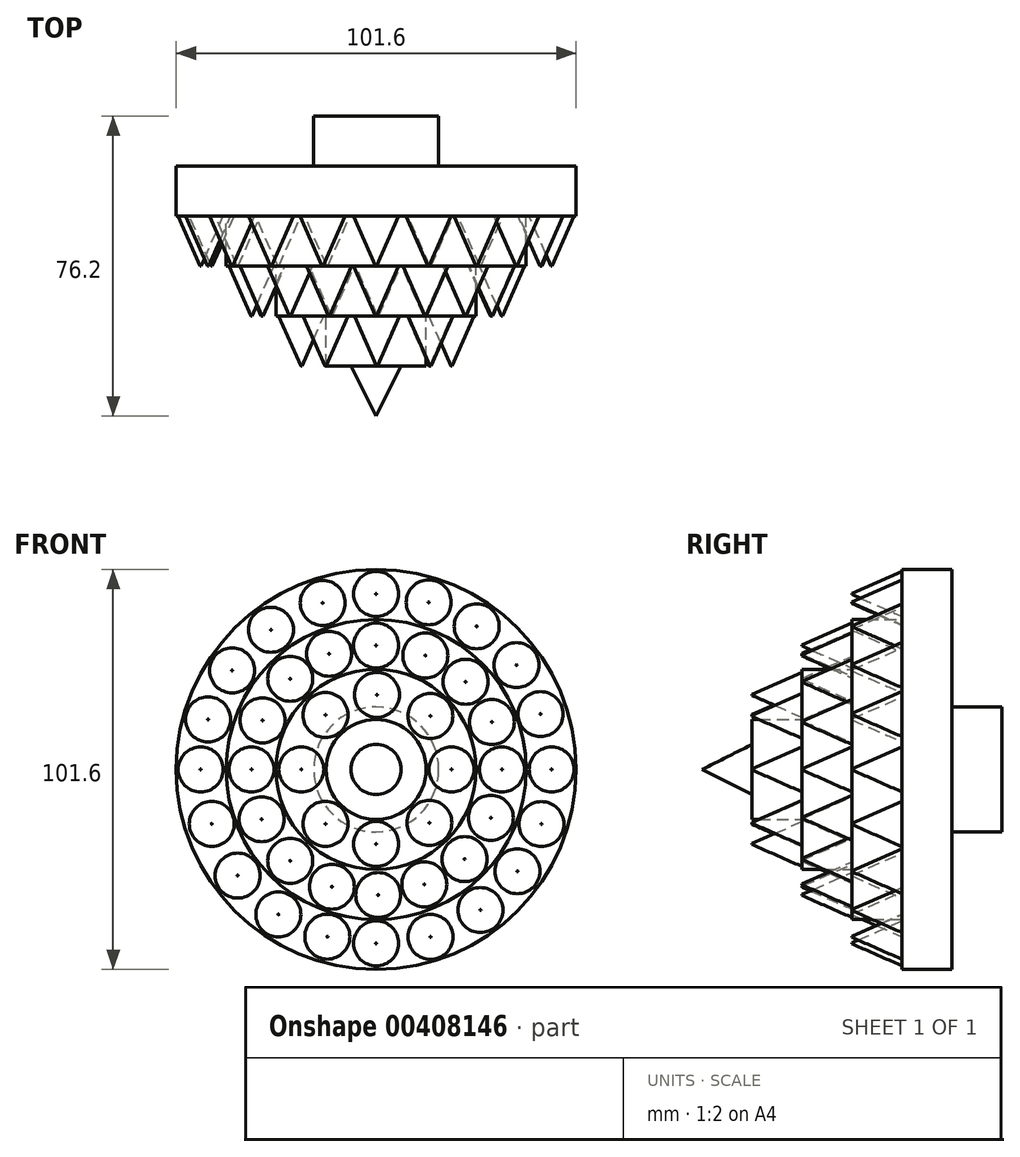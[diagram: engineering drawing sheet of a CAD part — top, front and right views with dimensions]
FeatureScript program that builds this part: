
annotation { "Feature Type Name" : "Feature", "Feature Type Description" : "" }
export const myFeature = defineFeature(function(context is Context, id is Id, definition is map)
    precondition{}
    {
        {
            var Q0;
            Q0=qCreatedBy(makeId("Front.planeOp"),FACE);
            var sketch = newSketch(context, id + "F0", { "sketchPlane" : qUnion([Q0])});
            skCircle(sketch, "E0", {"center": v(0, 0) * mm, "radius": 15.88 * mm});
            skSolve(sketch);
        }
        {
            var Q0;
            Q0=qSketchRegion(id+"F0",true);
            extrude(context, id + "F1", {"entities" : qUnion([Q0]), "depth" : 12.7 * mm});
        }
        {
            var Q0;
            Q0=makeQuery(id+"F1.opExtrude","CAP_FACE",FACE,{"disambiguationData":[OSD([sQuery(id+"F0.wireOp",EDGE,"E0")])],"isStart":false});
            var sketch = newSketch(context, id + "F2", { "sketchPlane" : qUnion([Q0])});
            skCircle(sketch, "E1", {"center": v(0, 0) * mm, "radius": 50.8 * mm});
            skSolve(sketch);
        }
        {
            var Q0;
            Q0=qSketchRegion(id+"F2",true);
            extrude(context, id + "F3", {"entities" : qUnion([Q0]), "operationType" : NewBodyOperationType.ADD, "depth" : 12.7 * mm});
        }
        {
            var Q0;
            Q0=makeQuery(id+"F3.opExtrude","CAP_FACE",FACE,{"disambiguationData":[OSD([sQuery(id+"F2.wireOp",EDGE,"E1")])],"isStart":false});
            var sketch = newSketch(context, id + "F4", { "sketchPlane" : qUnion([Q0])});
            skCircle(sketch, "E2", {"center": v(0, 0) * mm, "radius": 38.1 * mm});
            skSolve(sketch);
        }
        {
            var Q0;
            Q0=qSketchRegion(id+"F4",true);
            extrude(context, id + "F5", {"entities" : qUnion([Q0]), "operationType" : NewBodyOperationType.ADD, "depth" : 12.7 * mm});
        }
        {
            var Q0;
            Q0=makeQuery(id+"F5.opExtrude","CAP_FACE",FACE,{"disambiguationData":[OSD([sQuery(id+"F4.wireOp",EDGE,"E2")])],"isStart":false});
            var sketch = newSketch(context, id + "F6", { "sketchPlane" : qUnion([Q0])});
            skCircle(sketch, "E3", {"center": v(0, 0) * mm, "radius": 25.4 * mm});
            skSolve(sketch);
        }
        {
            var Q0;
            Q0=qSketchRegion(id+"F6",true);
            extrude(context, id + "F7", {"entities" : qUnion([Q0]), "operationType" : NewBodyOperationType.ADD, "depth" : 12.7 * mm});
        }
        {
            var Q0;
            Q0=makeQuery(id+"F7.opExtrude","CAP_FACE",FACE,{"disambiguationData":[OSD([sQuery(id+"F6.wireOp",EDGE,"E3")])],"isStart":false});
            var sketch = newSketch(context, id + "F8", { "sketchPlane" : qUnion([Q0])});
            skCircle(sketch, "E4", {"center": v(0, 0) * mm, "radius": 12.7 * mm});
            skSolve(sketch);
        }
        {
            var Q0;
            Q0=qSketchRegion(id+"F8",true);
            extrude(context, id + "F9", {"entities" : qUnion([Q0]), "operationType" : NewBodyOperationType.ADD, "depth" : 12.7 * mm});
        }
        {
            var Q0;
            Q0=makeQuery(id+"F9.opExtrude","CAP_FACE",FACE,{"disambiguationData":[OSD([sQuery(id+"F8.wireOp",EDGE,"E4")])],"isStart":false});
            var sketch = newSketch(context, id + "F10", { "sketchPlane" : qUnion([Q0])});
            skCircle(sketch, "E5", {"center": v(0, 0) * mm, "radius": 6.35 * mm});
            skSolve(sketch);
        }
        {
            var Q0;
            Q0=qSketchRegion(id+"F10",true);
            extrude(context, id + "F11", {"entities" : qUnion([Q0]), "operationType" : NewBodyOperationType.ADD, "depth" : 12.7 * mm});
        }
        {
            var Q0;
            Q0=makeQuery(id+"F11.opExtrude","CAP_EDGE",EDGE,{"disambiguationData":[OSD([sQuery(id+"F10.wireOp",EDGE,"E5")])],"isStart":false});
            chamfer(context, id + "F12", {"entities" : qUnion([Q0]), "chamferType" : ChamferType.TWO_OFFSETS, "width1" : 6.35 * mm, "oppositeDirection" : false, "width2" : 12.7 * mm, "tangentPropagation" : true});
        }
        {
            var Q0;
            Q0=makeQuery(id+"F3.opExtrude","CAP_FACE",FACE,{"disambiguationData":[OSD([sQuery(id+"F2.wireOp",EDGE,"E1")])],"isStart":false});
            var sketch = newSketch(context, id + "F13", { "sketchPlane" : qUnion([Q0])});
            skCircle(sketch, "E6", {"center": v(25.56, 36.37) * mm, "radius": 5.72 * mm});
            skCircle(sketch, "E7", {"center": v(35.65, 26.5) * mm, "radius": 5.72 * mm});
            skCircle(sketch, "E8", {"center": v(41.76, 14.06) * mm, "radius": 5.72 * mm});
            skCircle(sketch, "E9", {"center": v(44.58, 0) * mm, "radius": 5.72 * mm});
            skCircle(sketch, "E10", {"center": v(42, -13.89) * mm, "radius": 5.72 * mm});
            skCircle(sketch, "E11", {"center": v(35.89, -25.86) * mm, "radius": 5.72 * mm});
            skCircle(sketch, "E12", {"center": v(26.5, -35.73) * mm, "radius": 5.72 * mm});
            skCircle(sketch, "E13", {"center": v(13.34, 42.47) * mm, "radius": 5.72 * mm});
            skCircle(sketch, "E14", {"center": v(0, 44.59) * mm, "radius": 5.72 * mm});
            skCircle(sketch, "E15", {"center": v(0, -44.18) * mm, "radius": 5.72 * mm});
            skCircle(sketch, "E16", {"center": v(13.81, -42.54) * mm, "radius": 5.72 * mm});
            skCircle(sketch, "E17", {"center": v(-12.4, -42.47) * mm, "radius": 5.72 * mm});
            skCircle(sketch, "E18", {"center": v(-24.85, -36.84) * mm, "radius": 5.72 * mm});
            skCircle(sketch, "E19", {"center": v(-35.18, -26.98) * mm, "radius": 5.72 * mm});
            skCircle(sketch, "E20", {"center": v(-41.76, -13.82) * mm, "radius": 5.72 * mm});
            skCircle(sketch, "E21", {"center": v(-44.58, 0) * mm, "radius": 5.72 * mm});
            skCircle(sketch, "E22", {"center": v(-42.7, 12.71) * mm, "radius": 5.72 * mm});
            skCircle(sketch, "E23", {"center": v(-36.6, 25.16) * mm, "radius": 5.72 * mm});
            skCircle(sketch, "E24", {"center": v(-26.73, 35.5) * mm, "radius": 5.72 * mm});
            skCircle(sketch, "E25", {"center": v(-13.58, 42.3) * mm, "radius": 5.72 * mm});
            skSolve(sketch);
        }
        {
            var Q0;
            Q0=qSketchRegion(id+"F13",true);
            extrude(context, id + "F14", {"entities" : qUnion([Q0]), "operationType" : NewBodyOperationType.ADD, "depth" : 12.7 * mm});
        }
        {
            var Q0;
            Q0=makeQuery(id+"F14.opExtrude","CAP_EDGE",EDGE,{"disambiguationData":[OSD([sQuery(id+"F13.wireOp",EDGE,"E20")])],"isStart":false});
            var Q1;
            Q1=makeQuery(id+"F14.opExtrude","CAP_EDGE",EDGE,{"disambiguationData":[OSD([sQuery(id+"F13.wireOp",EDGE,"E21")])],"isStart":false});
            var Q2;
            Q2=makeQuery(id+"F14.opExtrude","CAP_EDGE",EDGE,{"disambiguationData":[OSD([sQuery(id+"F13.wireOp",EDGE,"E22")])],"isStart":false});
            var Q3;
            Q3=makeQuery(id+"F14.opExtrude","CAP_EDGE",EDGE,{"disambiguationData":[OSD([sQuery(id+"F13.wireOp",EDGE,"E23")])],"isStart":false});
            var Q4;
            Q4=makeQuery(id+"F14.opExtrude","CAP_EDGE",EDGE,{"disambiguationData":[OSD([sQuery(id+"F13.wireOp",EDGE,"E24")])],"isStart":false});
            var Q5;
            Q5=makeQuery(id+"F14.opExtrude","CAP_EDGE",EDGE,{"disambiguationData":[OSD([sQuery(id+"F13.wireOp",EDGE,"E25")])],"isStart":false});
            var Q6;
            Q6=makeQuery(id+"F14.opExtrude","CAP_EDGE",EDGE,{"disambiguationData":[OSD([sQuery(id+"F13.wireOp",EDGE,"E14")])],"isStart":false});
            var Q7;
            Q7=makeQuery(id+"F14.opExtrude","CAP_EDGE",EDGE,{"disambiguationData":[OSD([sQuery(id+"F13.wireOp",EDGE,"E13")])],"isStart":false});
            var Q8;
            Q8=makeQuery(id+"F14.opExtrude","CAP_EDGE",EDGE,{"disambiguationData":[OSD([sQuery(id+"F13.wireOp",EDGE,"E6")])],"isStart":false});
            var Q9;
            Q9=makeQuery(id+"F14.opExtrude","CAP_EDGE",EDGE,{"disambiguationData":[OSD([sQuery(id+"F13.wireOp",EDGE,"E7")])],"isStart":false});
            var Q10;
            Q10=makeQuery(id+"F14.opExtrude","CAP_EDGE",EDGE,{"disambiguationData":[OSD([sQuery(id+"F13.wireOp",EDGE,"E8")])],"isStart":false});
            var Q11;
            Q11=makeQuery(id+"F14.opExtrude","CAP_EDGE",EDGE,{"disambiguationData":[OSD([sQuery(id+"F13.wireOp",EDGE,"E9")])],"isStart":false});
            var Q12;
            Q12=makeQuery(id+"F14.opExtrude","CAP_EDGE",EDGE,{"disambiguationData":[OSD([sQuery(id+"F13.wireOp",EDGE,"E10")])],"isStart":false});
            var Q13;
            Q13=makeQuery(id+"F14.opExtrude","CAP_EDGE",EDGE,{"disambiguationData":[OSD([sQuery(id+"F13.wireOp",EDGE,"E11")])],"isStart":false});
            var Q14;
            Q14=makeQuery(id+"F14.opExtrude","CAP_EDGE",EDGE,{"disambiguationData":[OSD([sQuery(id+"F13.wireOp",EDGE,"E12")])],"isStart":false});
            var Q15;
            Q15=makeQuery(id+"F14.opExtrude","CAP_EDGE",EDGE,{"disambiguationData":[OSD([sQuery(id+"F13.wireOp",EDGE,"E16")])],"isStart":false});
            var Q16;
            Q16=makeQuery(id+"F14.opExtrude","CAP_EDGE",EDGE,{"disambiguationData":[OSD([sQuery(id+"F13.wireOp",EDGE,"E15")])],"isStart":false});
            var Q17;
            Q17=makeQuery(id+"F14.opExtrude","CAP_EDGE",EDGE,{"disambiguationData":[OSD([sQuery(id+"F13.wireOp",EDGE,"E17")])],"isStart":false});
            var Q18;
            Q18=makeQuery(id+"F14.opExtrude","CAP_EDGE",EDGE,{"disambiguationData":[OSD([sQuery(id+"F13.wireOp",EDGE,"E18")])],"isStart":false});
            var Q19;
            Q19=makeQuery(id+"F14.opExtrude","CAP_EDGE",EDGE,{"disambiguationData":[OSD([sQuery(id+"F13.wireOp",EDGE,"E19")])],"isStart":false});
            chamfer(context, id + "F15", {"entities" : qUnion([Q0, Q1, Q2, Q3, Q4, Q5, Q6, Q7, Q8, Q9, Q10, Q11, Q12, Q13, Q14, Q15, Q16, Q17, Q18, Q19]), "chamferType" : ChamferType.TWO_OFFSETS, "width1" : 5.6 * mm, "oppositeDirection" : false, "width2" : 12.7 * mm, "tangentPropagation" : true});
        }
        {
            var Q0;
            Q0=makeQuery(id+"F5.opExtrude","CAP_FACE",FACE,{"disambiguationData":[OSD([sQuery(id+"F4.wireOp",EDGE,"E2")])],"isStart":false});
            var sketch = newSketch(context, id + "F16", { "sketchPlane" : qUnion([Q0])});
            skCircle(sketch, "E26", {"center": v(-31.68, 0) * mm, "radius": 5.72 * mm});
            skCircle(sketch, "E27", {"center": v(0, 31.5) * mm, "radius": 5.72 * mm});
            skCircle(sketch, "E28", {"center": v(0.51, -31.9) * mm, "radius": 5.72 * mm});
            skCircle(sketch, "E29", {"center": v(31.95, 0) * mm, "radius": 5.72 * mm});
            skCircle(sketch, "E30", {"center": v(29.39, 12.04) * mm, "radius": 5.72 * mm});
            skCircle(sketch, "E31", {"center": v(22.73, 22.29) * mm, "radius": 5.72 * mm});
            skCircle(sketch, "E32", {"center": v(12.48, 28.95) * mm, "radius": 5.72 * mm});
            skCircle(sketch, "E33", {"center": v(29.13, -12.29) * mm, "radius": 5.72 * mm});
            skCircle(sketch, "E34", {"center": v(22.47, -22.79) * mm, "radius": 5.72 * mm});
            skCircle(sketch, "E35", {"center": v(12.23, -29.19) * mm, "radius": 5.72 * mm});
            skCircle(sketch, "E36", {"center": v(-11.25, -29.8) * mm, "radius": 5.72 * mm});
            skCircle(sketch, "E37", {"center": v(-21.82, -23.22) * mm, "radius": 5.72 * mm});
            skCircle(sketch, "E38", {"center": v(-29.1, -12.65) * mm, "radius": 5.72 * mm});
            skCircle(sketch, "E39", {"center": v(-28.86, 12.48) * mm, "radius": 5.72 * mm});
            skCircle(sketch, "E40", {"center": v(-21.82, 23.05) * mm, "radius": 5.72 * mm});
            skCircle(sketch, "E41", {"center": v(-11.96, 29.39) * mm, "radius": 5.72 * mm});
            skSolve(sketch);
        }
        {
            var Q0;
            Q0=qSketchRegion(id+"F16",true);
            extrude(context, id + "F17", {"entities" : qUnion([Q0]), "operationType" : NewBodyOperationType.ADD, "depth" : 12.7 * mm});
        }
        {
            var Q0;
            Q0=makeQuery(id+"F17.opExtrude","CAP_EDGE",EDGE,{"disambiguationData":[OSD([sQuery(id+"F16.wireOp",EDGE,"E33")])],"isStart":false});
            var Q1;
            Q1=makeQuery(id+"F17.opExtrude","CAP_EDGE",EDGE,{"disambiguationData":[OSD([sQuery(id+"F16.wireOp",EDGE,"E29")])],"isStart":false});
            var Q2;
            Q2=makeQuery(id+"F17.opExtrude","CAP_EDGE",EDGE,{"disambiguationData":[OSD([sQuery(id+"F16.wireOp",EDGE,"E30")])],"isStart":false});
            var Q3;
            Q3=makeQuery(id+"F17.opExtrude","CAP_EDGE",EDGE,{"disambiguationData":[OSD([sQuery(id+"F16.wireOp",EDGE,"E31")])],"isStart":false});
            var Q4;
            Q4=makeQuery(id+"F17.opExtrude","CAP_EDGE",EDGE,{"disambiguationData":[OSD([sQuery(id+"F16.wireOp",EDGE,"E32")])],"isStart":false});
            var Q5;
            Q5=makeQuery(id+"F17.opExtrude","CAP_EDGE",EDGE,{"disambiguationData":[OSD([sQuery(id+"F16.wireOp",EDGE,"E27")])],"isStart":false});
            var Q6;
            Q6=makeQuery(id+"F17.opExtrude","CAP_EDGE",EDGE,{"disambiguationData":[OSD([sQuery(id+"F16.wireOp",EDGE,"E41")])],"isStart":false});
            var Q7;
            Q7=makeQuery(id+"F17.opExtrude","CAP_EDGE",EDGE,{"disambiguationData":[OSD([sQuery(id+"F16.wireOp",EDGE,"E40")])],"isStart":false});
            var Q8;
            Q8=makeQuery(id+"F17.opExtrude","CAP_EDGE",EDGE,{"disambiguationData":[OSD([sQuery(id+"F16.wireOp",EDGE,"E39")])],"isStart":false});
            var Q9;
            Q9=makeQuery(id+"F17.opExtrude","CAP_EDGE",EDGE,{"disambiguationData":[OSD([sQuery(id+"F16.wireOp",EDGE,"E26")])],"isStart":false});
            var Q10;
            Q10=makeQuery(id+"F17.opExtrude","CAP_EDGE",EDGE,{"disambiguationData":[OSD([sQuery(id+"F16.wireOp",EDGE,"E38")])],"isStart":false});
            var Q11;
            Q11=makeQuery(id+"F17.opExtrude","CAP_EDGE",EDGE,{"disambiguationData":[OSD([sQuery(id+"F16.wireOp",EDGE,"E37")])],"isStart":false});
            var Q12;
            Q12=makeQuery(id+"F17.opExtrude","CAP_EDGE",EDGE,{"disambiguationData":[OSD([sQuery(id+"F16.wireOp",EDGE,"E36")])],"isStart":false});
            var Q13;
            Q13=makeQuery(id+"F17.opExtrude","CAP_EDGE",EDGE,{"disambiguationData":[OSD([sQuery(id+"F16.wireOp",EDGE,"E28")])],"isStart":false});
            var Q14;
            Q14=makeQuery(id+"F17.opExtrude","CAP_EDGE",EDGE,{"disambiguationData":[OSD([sQuery(id+"F16.wireOp",EDGE,"E35")])],"isStart":false});
            var Q15;
            Q15=makeQuery(id+"F17.opExtrude","CAP_EDGE",EDGE,{"disambiguationData":[OSD([sQuery(id+"F16.wireOp",EDGE,"E34")])],"isStart":false});
            chamfer(context, id + "F18", {"entities" : qUnion([Q0, Q1, Q2, Q3, Q4, Q5, Q6, Q7, Q8, Q9, Q10, Q11, Q12, Q13, Q14, Q15]), "chamferType" : ChamferType.TWO_OFFSETS, "width1" : 5.6 * mm, "oppositeDirection" : false, "width2" : 12.7 * mm, "tangentPropagation" : true});
        }
        {
            var Q0;
            Q0=makeQuery(id+"F7.opExtrude","CAP_FACE",FACE,{"disambiguationData":[OSD([sQuery(id+"F6.wireOp",EDGE,"E3")])],"isStart":false});
            var sketch = newSketch(context, id + "F19", { "sketchPlane" : qUnion([Q0])});
            skCircle(sketch, "E42", {"center": v(-19.02, 0) * mm, "radius": 5.72 * mm});
            skCircle(sketch, "E43", {"center": v(0.2, 18.96) * mm, "radius": 5.72 * mm});
            skCircle(sketch, "E44", {"center": v(19.14, 0) * mm, "radius": 5.72 * mm});
            skCircle(sketch, "E45", {"center": v(0, -18.94) * mm, "radius": 5.72 * mm});
            skCircle(sketch, "E46", {"center": v(-12.87, -13.82) * mm, "radius": 5.72 * mm});
            skCircle(sketch, "E47", {"center": v(-12.87, 13.84) * mm, "radius": 5.72 * mm});
            skCircle(sketch, "E48", {"center": v(13.77, 13.58) * mm, "radius": 5.72 * mm});
            skCircle(sketch, "E49", {"center": v(13.5, -13.57) * mm, "radius": 5.72 * mm});
            skSolve(sketch);
        }
        {
            var Q0;
            Q0=qSketchRegion(id+"F19",true);
            extrude(context, id + "F20", {"entities" : qUnion([Q0]), "operationType" : NewBodyOperationType.ADD, "depth" : 12.7 * mm});
        }
        {
            var Q0;
            Q0=makeQuery(id+"F20.opExtrude","CAP_EDGE",EDGE,{"disambiguationData":[OSD([sQuery(id+"F19.wireOp",EDGE,"E45")])],"isStart":false});
            var Q1;
            Q1=makeQuery(id+"F20.opExtrude","CAP_EDGE",EDGE,{"disambiguationData":[OSD([sQuery(id+"F19.wireOp",EDGE,"E46")])],"isStart":false});
            var Q2;
            Q2=makeQuery(id+"F20.opExtrude","CAP_EDGE",EDGE,{"disambiguationData":[OSD([sQuery(id+"F19.wireOp",EDGE,"E42")])],"isStart":false});
            var Q3;
            Q3=makeQuery(id+"F20.opExtrude","CAP_EDGE",EDGE,{"disambiguationData":[OSD([sQuery(id+"F19.wireOp",EDGE,"E47")])],"isStart":false});
            var Q4;
            Q4=makeQuery(id+"F20.opExtrude","CAP_EDGE",EDGE,{"disambiguationData":[OSD([sQuery(id+"F19.wireOp",EDGE,"E43")])],"isStart":false});
            var Q5;
            Q5=makeQuery(id+"F20.opExtrude","CAP_EDGE",EDGE,{"disambiguationData":[OSD([sQuery(id+"F19.wireOp",EDGE,"E48")])],"isStart":false});
            var Q6;
            Q6=makeQuery(id+"F20.opExtrude","CAP_EDGE",EDGE,{"disambiguationData":[OSD([sQuery(id+"F19.wireOp",EDGE,"E44")])],"isStart":false});
            var Q7;
            Q7=makeQuery(id+"F20.opExtrude","CAP_EDGE",EDGE,{"disambiguationData":[OSD([sQuery(id+"F19.wireOp",EDGE,"E49")])],"isStart":false});
            chamfer(context, id + "F21", {"entities" : qUnion([Q0, Q1, Q2, Q3, Q4, Q5, Q6, Q7]), "chamferType" : ChamferType.TWO_OFFSETS, "width1" : 5.6 * mm, "oppositeDirection" : false, "width2" : 12.7 * mm, "tangentPropagation" : true});
        }
    });
